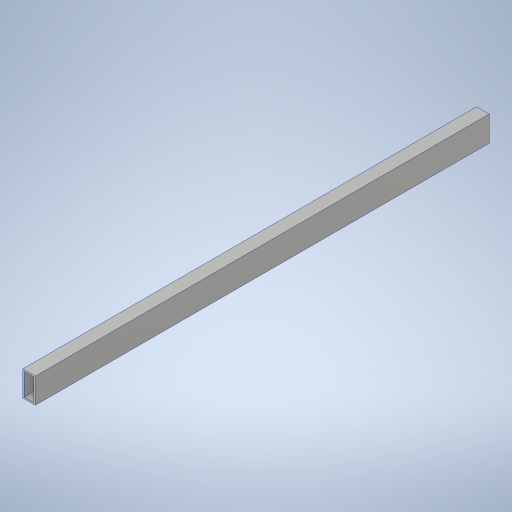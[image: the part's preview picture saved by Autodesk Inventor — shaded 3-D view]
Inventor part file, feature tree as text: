
AUTODESK INVENTOR PART (.ipt)
format: ipt  version: 2023.4 (Build 274418000, 418)  size: 242,688 bytes
history: native  units: in
note: dims shown in document units (in); Inventor stores cm internally (conversion verified against a paired STEP export)
features: extrude x1
ambient origin geometry x8: Origin, YZ Plane, XZ Plane, XY Plane, X Axis, Y Axis, Z Axis, Center Point
bodies: Solid1 (feature_tree)
feature tree (1):
  extrude  "Extrusion1"  TaperAngle=0.0deg  [1 undecoded]
note: 1 required parameter value undecoded (feature->parameter linkage not recoverable at this tier; creation-order binding heuristic only, values carry confidence <= 0.55)
